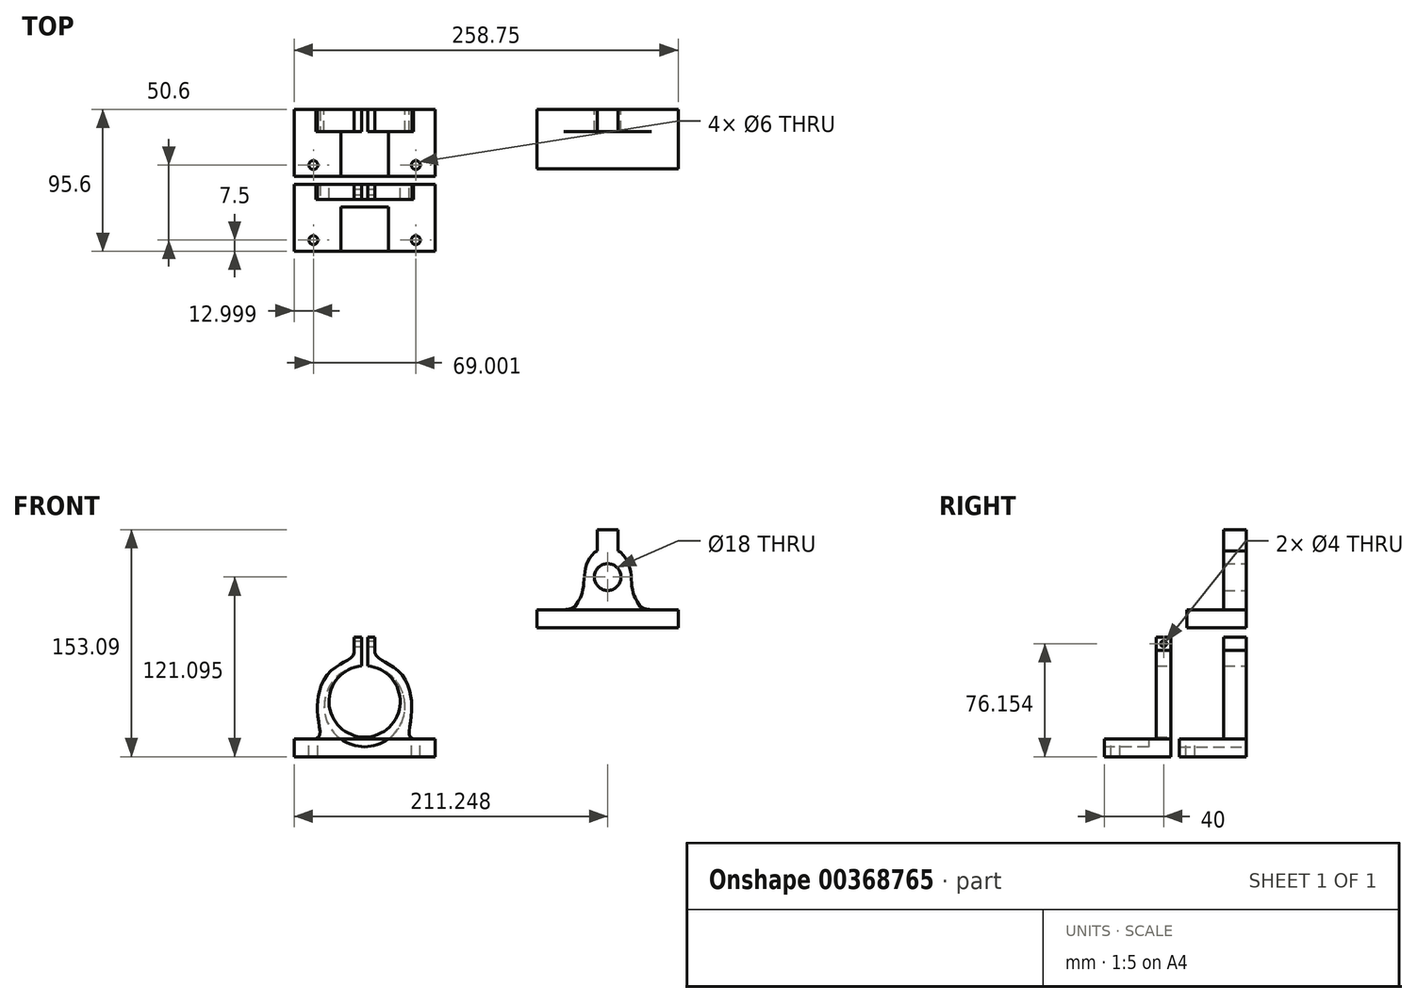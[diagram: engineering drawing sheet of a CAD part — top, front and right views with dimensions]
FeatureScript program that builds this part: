
annotation { "Feature Type Name" : "Feature", "Feature Type Description" : "" }
export const myFeature = defineFeature(function(context is Context, id is Id, definition is map)
    precondition{}
    {
        {
            var Q0;
            Q0=qCreatedBy(makeId("Front.planeOp"),FACE);
            var sketch = newSketch(context, id + "F0", { "sketchPlane" : qUnion([Q0])});
            skLineSegment(sketch, "E0", {"start": v(-93.8, 148.82) * mm, "end": v(-100.8, 148.82) * mm});
            skLineSegment(sketch, "E1", {"start": v(-100.8, 148.82) * mm, "end": v(-100.8, 134.43) * mm});
            skFitSpline(sketch, "E2", {"points": [v(-100.8, 134.43) * mm, v(-106.63, 128.23) * mm, v(-109.38, 119.14) * mm, v(-110.23, 109.7) * mm, v(-112.07, 103.39) * mm, v(-113.8, 99.96) * mm, v(-117.07, 96.12) * mm, v(-123.3, 94.82) * mm], "startDerivative": vector(-41.03, -17.29) * mm, "endDerivative": vector(-26.14, 0) * mm});
            skLineSegment(sketch, "E3", {"start": v(-123.3, 94.82) * mm, "end": v(-141.3, 94.82) * mm});
            skLineSegment(sketch, "E4", {"start": v(-141.3, 94.82) * mm, "end": v(-141.3, 82.82) * mm});
            skLineSegment(sketch, "E5", {"start": v(-141.3, 82.82) * mm, "end": v(-93.8, 82.82) * mm});
            skLineSegment(sketch, "E6", {"start": v(-93.8, 82.82) * mm, "end": v(-93.8, 107.82) * mm});
            skArc(sketch, "E7", {"start": v(-93.8, 125.82) * mm, "mid": v(-102.8, 116.82) * mm, "end": v(-93.8, 107.82) * mm});
            skLineSegment(sketch, "E8", {"start": v(-93.8, 125.82) * mm, "end": v(-93.8, 148.82) * mm});
            skPoint(sketch, "E9", {"position": v(-128.3, 94.82) * mm});
            skLineSegment(sketch, "E10.MirrorCS", {"start": v(-93.8, 148.82) * mm, "end": v(-86.8, 148.82) * mm});
            skLineSegment(sketch, "E11.MirrorCS", {"start": v(-46.3, 82.82) * mm, "end": v(-93.8, 82.82) * mm});
            skLineSegment(sketch, "E12.MirrorCS", {"start": v(-46.3, 94.82) * mm, "end": v(-46.3, 82.82) * mm});
            skLineSegment(sketch, "E13.MirrorCS", {"start": v(-64.3, 94.82) * mm, "end": v(-46.3, 94.82) * mm});
            skFitSpline(sketch, "E14.MirrorCS", {"points": [v(-86.8, 134.43) * mm, v(-80.95, 128.23) * mm, v(-78.2, 119.14) * mm, v(-77.35, 109.7) * mm, v(-75.52, 103.39) * mm, v(-73.79, 99.96) * mm, v(-70.5, 96.12) * mm, v(-64.3, 94.82) * mm], "startDerivative": vector(41.03, -17.29) * mm, "endDerivative": vector(26.14, 0) * mm});
            skLineSegment(sketch, "E15.MirrorCS", {"start": v(-86.8, 148.82) * mm, "end": v(-86.8, 134.43) * mm});
            skArc(sketch, "E16.MirrorCS", {"start": v(-93.8, 125.82) * mm, "mid": v(-84.8, 116.82) * mm, "end": v(-93.8, 107.82) * mm});
            skPoint(sketch, "E17.MirrorP", {"position": v(-59.3, 94.82) * mm});
            skCircle(sketch, "E18", {"center": v(-257.54, 29.73) * mm, "radius": 27.25 * mm});
            skFitSpline(sketch, "E19", {"points": [v(-290.46, 7.73) * mm, v(-287.85, 9.94) * mm, v(-287.98, 16.09) * mm, v(-289.33, 27.52) * mm, v(-288.47, 37.36) * mm, v(-283.92, 49.4) * mm, v(-274.33, 57.89) * mm, v(-268.3, 61.2) * mm, v(-264.74, 65.02) * mm, v(-264.54, 67.48) * mm], "startDerivative": vector(50.74, 19) * mm, "endDerivative": vector(1.63, 36.85) * mm});
            skLineSegment(sketch, "E20", {"start": v(-264.54, 67.48) * mm, "end": v(-264.54, 76.3) * mm});
            skLineSegment(sketch, "E21", {"start": v(-264.54, 76.3) * mm, "end": v(-259.54, 76.3) * mm});
            skLineSegment(sketch, "E22", {"start": v(-259.54, 76.3) * mm, "end": v(-259.54, 56.9) * mm});
            skLineSegment(sketch, "E23", {"start": v(-290.46, 7.73) * mm, "end": v(-305.04, 7.73) * mm});
            skLineSegment(sketch, "E24", {"start": v(-305.04, 7.73) * mm, "end": v(-305.04, -4.27) * mm});
            skLineSegment(sketch, "E25", {"start": v(-305.04, -4.27) * mm, "end": v(-257.6, -4.27) * mm});
            skLineSegment(sketch, "E26", {"start": v(-257.6, -4.27) * mm, "end": v(-257.6, 2.48) * mm});
            skLineSegment(sketch, "E27.MirrorCS", {"start": v(-250.54, 67.48) * mm, "end": v(-250.54, 76.3) * mm});
            skLineSegment(sketch, "E28.MirrorCS", {"start": v(-250.54, 76.3) * mm, "end": v(-255.54, 76.3) * mm});
            skLineSegment(sketch, "E29.MirrorCS", {"start": v(-255.54, 76.3) * mm, "end": v(-255.54, 56.9) * mm});
            skLineSegment(sketch, "E30.MirrorCS", {"start": v(-210.04, -4.27) * mm, "end": v(-257.48, -4.27) * mm});
            skLineSegment(sketch, "E31.MirrorCS", {"start": v(-210.04, 7.73) * mm, "end": v(-210.04, -4.27) * mm});
            skFitSpline(sketch, "E32.MirrorCS", {"points": [v(-224.63, 7.73) * mm, v(-227.23, 9.94) * mm, v(-227.1, 16.09) * mm, v(-225.75, 27.52) * mm, v(-226.61, 37.36) * mm, v(-231.16, 49.4) * mm, v(-240.75, 57.89) * mm, v(-246.78, 61.2) * mm, v(-250.34, 65.02) * mm, v(-250.54, 67.48) * mm], "startDerivative": vector(-50.74, 19) * mm, "endDerivative": vector(-1.63, 36.85) * mm});
            skLineSegment(sketch, "E33.MirrorCS", {"start": v(-224.63, 7.73) * mm, "end": v(-210.04, 7.73) * mm});
            skLineSegment(sketch, "E34", {"start": v(-305.04, -4.27) * mm, "end": v(-210.04, -4.27) * mm});
            skSolve(sketch);
        }
        {
            var Q0;
            Q0=makeQuery(id+"F0.imprint","IMPRINT",FACE,{"disambiguationData":[TD([[makeQuery(id+"F0.imprint","IMPRINT",EDGE,{"derivedFrom":sQuery(id+"F0.wireOp",EDGE,"E6")}),-1.0]])]});
            var Q1;
            Q1=makeQuery(id+"F0.imprint","IMPRINT",FACE,{"disambiguationData":[TD([[makeQuery(id+"F0.imprint","IMPRINT",EDGE,{"derivedFrom":sQuery(id+"F0.wireOp",EDGE,"E0")}),1.0]])]});
            var Q2;
            Q2=makeQuery(id+"F0.imprint","IMPRINT",FACE,{"disambiguationData":[TD([[makeQuery(id+"F0.imprint","IMPRINT",EDGE,{"derivedFrom":sQuery(id+"F0.wireOp",EDGE,"E19")}),-1.0]])]});
            var Q3;
            {var subQ1=sQuery(id+"F0.wireOp",EDGE,"E26");Q3=makeQuery(id+"F0.imprint","IMPRINT",FACE,{"disambiguationData":[TD([[makeQuery(id+"F0.imprint","IMPRINT",EDGE,{"derivedFrom":subQ1}),-1.0]])]});}
            extrude(context, id + "F1", {"entities" : qUnion([Q0, Q1, Q2, Q3]), "depth" : 15 * mm, "offsetDistance" : 25 * mm});
        }
        {
            var Q0;
            Q0=makeQuery(id+"F1.opExtrude","CAP_FACE",FACE,{"disambiguationData":[OSD([sQuery(id+"F0.wireOp",EDGE,"E0"),sQuery(id+"F0.wireOp",EDGE,"E1"),sQuery(id+"F0.wireOp",EDGE,"E2"),sQuery(id+"F0.wireOp",EDGE,"E3"),sQuery(id+"F0.wireOp",EDGE,"E4"),sQuery(id+"F0.wireOp",EDGE,"E5"),sQuery(id+"F0.wireOp",EDGE,"E7"),sQuery(id+"F0.wireOp",EDGE,"E10.MirrorCS"),sQuery(id+"F0.wireOp",EDGE,"E11.MirrorCS"),sQuery(id+"F0.wireOp",EDGE,"E12.MirrorCS"),sQuery(id+"F0.wireOp",EDGE,"E13.MirrorCS"),sQuery(id+"F0.wireOp",EDGE,"E14.MirrorCS"),sQuery(id+"F0.wireOp",EDGE,"E15.MirrorCS"),sQuery(id+"F0.wireOp",EDGE,"E16.MirrorCS")])],"isStart":false});
            var sketch = newSketch(context, id + "F2", { "sketchPlane" : qUnion([Q0])});
            skLineSegment(sketch, "E35.bottom", {"start": v(-141.3, 82.82) * mm, "end": v(-46.3, 82.82) * mm});
            skLineSegment(sketch, "E35.top", {"start": v(-141.3, 94.82) * mm, "end": v(-46.3, 94.82) * mm});
            skLineSegment(sketch, "E35.left", {"start": v(-141.3, 82.82) * mm, "end": v(-141.3, 94.82) * mm});
            skLineSegment(sketch, "E35.right", {"start": v(-46.3, 82.82) * mm, "end": v(-46.3, 94.82) * mm});
            skSolve(sketch);
        }
        {
            var Q0;
            Q0 = qSketchRegion(id + "F2", true);
            extrude(context, id + "F3", {"entities" : qUnion([Q0]), "operationType" : NewBodyOperationType.ADD, "depth" : 25 * mm, "offsetDistance" : 25 * mm});
        }
        {
            var Q0;
            Q0=makeQuery(id+"F1.opExtrude","CAP_FACE",FACE,{"disambiguationData":[OSD([sQuery(id+"F0.wireOp",EDGE,"E19"),sQuery(id+"F0.wireOp",EDGE,"E20"),sQuery(id+"F0.wireOp",EDGE,"E21"),sQuery(id+"F0.wireOp",EDGE,"E22"),sQuery(id+"F0.wireOp",EDGE,"E23"),sQuery(id+"F0.wireOp",EDGE,"E24"),sQuery(id+"F0.wireOp",EDGE,"E29.MirrorCS"),sQuery(id+"F0.wireOp",EDGE,"E27.MirrorCS"),sQuery(id+"F0.wireOp",EDGE,"E28.MirrorCS"),sQuery(id+"F0.wireOp",EDGE,"E31.MirrorCS"),sQuery(id+"F0.wireOp",EDGE,"E32.MirrorCS"),sQuery(id+"F0.wireOp",EDGE,"E18"),sQuery(id+"F0.wireOp",EDGE,"E33.MirrorCS"),sQuery(id+"F0.wireOp",EDGE,"E34")])],"isStart":false});
            var sketch = newSketch(context, id + "F4", { "sketchPlane" : qUnion([Q0])});
            skLineSegment(sketch, "E36.bottom", {"start": v(-305.04, -4.27) * mm, "end": v(-210.04, -4.27) * mm});
            skLineSegment(sketch, "E36.top", {"start": v(-305.04, 7.73) * mm, "end": v(-210.04, 7.73) * mm});
            skLineSegment(sketch, "E36.left", {"start": v(-305.04, -4.27) * mm, "end": v(-305.04, 7.73) * mm});
            skLineSegment(sketch, "E36.right", {"start": v(-210.04, -4.27) * mm, "end": v(-210.04, 7.73) * mm});
            skSolve(sketch);
        }
        {
            var Q0;
            Q0=makeQuery(id+"F4.imprint","IMPRINT",FACE,{"disambiguationData":[TD([[makeQuery(id+"F4.imprint","IMPRINT",EDGE,{"derivedFrom":sQuery(id+"F4.wireOp",EDGE,"E36.bottom")}),1.0]])]});
            extrude(context, id + "F5", {"entities" : qUnion([Q0]), "operationType" : NewBodyOperationType.ADD, "depth" : 30 * mm, "offsetDistance" : 25 * mm});
        }
        {
            var Q0;
            {var subQ0=sQuery(id+"F4.wireOp",EDGE,"E36.top");Q0=makeQuery(id+"F5.boolean.opBoolean","MERGE",FACE,{"derivedFrom":[makeQuery(id+"F1.opExtrude","SWEPT_FACE",FACE,{"disambiguationData":[OSD([sQuery(id+"F0.wireOp",EDGE,"E23")])]}),makeQuery(id+"F5.opExtrude","SWEPT_FACE",FACE,{"disambiguationData":[OSD([subQ0]),TDD([makeQuery(id+"F4.imprint","IMPRINT",EDGE,{"disambiguationData":[TD([[makeQuery(id+"F4.imprint","INTERSECT",VERTEX,{"disambiguationData":[OD(0.0)],"derivedFrom":[makeQuery(id+"F1.opExtrude","CAP_EDGE",EDGE,{"disambiguationData":[OSD([sQuery(id+"F0.wireOp",EDGE,"E18")])],"isStart":false}),subQ0]}),1.0]])],"derivedFrom":subQ0}),makeQuery(id+"F4.imprint","IMPRINT",EDGE,{"disambiguationData":[TD([[makeQuery(id+"F4.imprint","INTERSECT",VERTEX,{"derivedFrom":[subQ0,sQuery(id+"F4.wireOp",EDGE,"E36.left")]}),1.0]])],"derivedFrom":subQ0})])]})]});}
            var sketch = newSketch(context, id + "F6", { "sketchPlane" : qUnion([Q0])});
            skCircle(sketch, "E37", {"center": v(-292.04, -37.5) * mm, "radius": 3 * mm});
            skCircle(sketch, "E38", {"center": v(-223.04, -37.5) * mm, "radius": 3 * mm});
            skLineSegment(sketch, "E39.bottom", {"start": v(-305.04, -45) * mm, "end": v(-210.04, -45) * mm});
            skLineSegment(sketch, "E39.top", {"start": v(-305.04, -30) * mm, "end": v(-210.04, -30) * mm});
            skLineSegment(sketch, "E39.left", {"start": v(-305.04, -45) * mm, "end": v(-305.04, -30) * mm});
            skLineSegment(sketch, "E39.right", {"start": v(-210.04, -45) * mm, "end": v(-210.04, -30) * mm});
            skPoint(sketch, "E40", {"position": v(-305.04, -37.5) * mm});
            skSolve(sketch);
        }
        {
            var Q0;
            Q0=makeQuery(id+"F6.imprint","IMPRINT",FACE,{"disambiguationData":[TD([[makeQuery(id+"F6.imprint","IMPRINT",EDGE,{"derivedFrom":sQuery(id+"F6.wireOp",EDGE,"E37")}),1.0]])]});
            var Q1;
            Q1=makeQuery(id+"F6.imprint","IMPRINT",FACE,{"disambiguationData":[TD([[makeQuery(id+"F6.imprint","IMPRINT",EDGE,{"derivedFrom":sQuery(id+"F6.wireOp",EDGE,"E38")}),1.0]])]});
            extrude(context, id + "F7", {"entities" : qUnion([Q0, Q1]), "operationType" : NewBodyOperationType.REMOVE, "oppositeDirection" : true, "depth" : 25 * mm, "offsetDistance" : 25 * mm});
        }
        {
            var Q0;
            Q0=qCreatedBy(makeId("Front.planeOp"),FACE);
            cPlane(context, id + "F8", {"entities" : qUnion([Q0]), "cplaneType" : CPlaneType.OFFSET, "offset" : 50.6 * mm, "width" : 150 * mm, "height" : 150 * mm});
        }
        {
            var Q0;
            Q0=qCreatedBy(id+"F8.planeOp",FACE);
            var sketch = newSketch(context, id + "F9", { "sketchPlane" : qUnion([Q0])});
            skFitSpline(sketch, "E41", {"points": [v(-290.46, 7.73) * mm, v(-287.85, 9.94) * mm, v(-287.98, 16.09) * mm, v(-289.33, 27.52) * mm, v(-288.47, 37.36) * mm, v(-283.92, 49.4) * mm, v(-274.33, 57.89) * mm, v(-268.3, 61.2) * mm, v(-264.74, 65.02) * mm, v(-264.54, 67.48) * mm], "startDerivative": vector(50.74, 19) * mm, "endDerivative": vector(1.63, 36.85) * mm});
            skLineSegment(sketch, "E42", {"start": v(-264.54, 67.48) * mm, "end": v(-264.54, 76.3) * mm});
            skLineSegment(sketch, "E43", {"start": v(-264.54, 76.3) * mm, "end": v(-259.54, 76.3) * mm});
            skLineSegment(sketch, "E44", {"start": v(-259.54, 76.3) * mm, "end": v(-259.54, 56.9) * mm});
            skLineSegment(sketch, "E45", {"start": v(-290.46, 7.73) * mm, "end": v(-305.04, 7.73) * mm});
            skLineSegment(sketch, "E46", {"start": v(-305.04, 7.73) * mm, "end": v(-305.04, -4.27) * mm});
            skLineSegment(sketch, "E47", {"start": v(-305.04, -4.27) * mm, "end": v(-257.6, -4.27) * mm});
            skLineSegment(sketch, "E48.MirrorCS", {"start": v(-250.54, 67.48) * mm, "end": v(-250.54, 76.3) * mm});
            skLineSegment(sketch, "E49.MirrorCS", {"start": v(-250.54, 76.3) * mm, "end": v(-255.54, 76.3) * mm});
            skLineSegment(sketch, "E50.MirrorCS", {"start": v(-255.54, 76.3) * mm, "end": v(-255.54, 56.9) * mm});
            skLineSegment(sketch, "E51.MirrorCS", {"start": v(-210.04, -4.27) * mm, "end": v(-257.54, -4.27) * mm});
            skLineSegment(sketch, "E52.MirrorCS", {"start": v(-210.04, 7.73) * mm, "end": v(-210.04, -4.27) * mm});
            skFitSpline(sketch, "E53.MirrorCS", {"points": [v(-224.62, 7.73) * mm, v(-227.23, 9.94) * mm, v(-227.1, 16.09) * mm, v(-225.75, 27.52) * mm, v(-226.61, 37.36) * mm, v(-231.16, 49.4) * mm, v(-240.75, 57.89) * mm, v(-246.78, 61.2) * mm, v(-250.34, 65.02) * mm, v(-250.54, 67.48) * mm], "startDerivative": vector(-50.74, 19) * mm, "endDerivative": vector(-1.63, 36.85) * mm});
            skLineSegment(sketch, "E54.MirrorCS", {"start": v(-224.62, 7.73) * mm, "end": v(-210.04, 7.73) * mm});
            skLineSegment(sketch, "E55", {"start": v(-305.04, -4.27) * mm, "end": v(-210.04, -4.27) * mm});
            skArc(sketch, "E56", {"start": v(-259.54, 56.9) * mm, "mid": v(-257.54, 8.99) * mm, "end": v(-255.54, 56.9) * mm});
            skPoint(sketch, "E57.center.orphan", {"position": v(-257.54, 29.74) * mm});
            skLineSegment(sketch, "E58", {"start": v(-290.46, 7.73) * mm, "end": v(-224.62, 7.73) * mm});
            skSolve(sketch);
        }
        {
            var Q0;
            Q0=makeQuery(id+"F9.imprint","IMPRINT",FACE,{"disambiguationData":[TD([[makeQuery(id+"F9.imprint","IMPRINT",EDGE,{"derivedFrom":sQuery(id+"F9.wireOp",EDGE,"E41")}),-1.0]])]});
            extrude(context, id + "F10", {"entities" : qUnion([Q0]), "depth" : 10 * mm, "offsetDistance" : 25 * mm});
        }
        {
            var Q0;
            Q0=makeQuery(id+"F9.imprint","IMPRINT",FACE,{"disambiguationData":[TD([[makeQuery(id+"F9.imprint","IMPRINT",EDGE,{"derivedFrom":sQuery(id+"F9.wireOp",EDGE,"E45")}),1.0]])]});
            extrude(context, id + "F11", {"entities" : qUnion([Q0]), "operationType" : NewBodyOperationType.ADD, "depth" : 45 * mm, "offsetDistance" : 25 * mm});
        }
        {
            var Q0;
            Q0=makeQuery(id+"F11.opExtrude","SWEPT_FACE",FACE,{"disambiguationData":[OSD([sQuery(id+"F9.wireOp",EDGE,"E45"),sQuery(id+"F9.wireOp",EDGE,"E54.MirrorCS"),sQuery(id+"F9.wireOp",EDGE,"E58")])]});
            var sketch = newSketch(context, id + "F12", { "sketchPlane" : qUnion([Q0])});
            skCircle(sketch, "E59", {"center": v(-292.04, -88.1) * mm, "radius": 3 * mm});
            skCircle(sketch, "E60", {"center": v(-223.04, -88.1) * mm, "radius": 3 * mm});
            skLineSegment(sketch, "E61.bottom", {"start": v(-305.04, -95.6) * mm, "end": v(-210.04, -95.6) * mm});
            skLineSegment(sketch, "E61.top", {"start": v(-305.04, -80.6) * mm, "end": v(-210.04, -80.6) * mm});
            skLineSegment(sketch, "E61.left", {"start": v(-305.04, -95.6) * mm, "end": v(-305.04, -80.6) * mm});
            skLineSegment(sketch, "E61.right", {"start": v(-210.04, -95.6) * mm, "end": v(-210.04, -80.6) * mm});
            skPoint(sketch, "E62", {"position": v(-305.04, -88.1) * mm});
            skSolve(sketch);
        }
        {
            var Q0;
            Q0=makeQuery(id+"F12.imprint","IMPRINT",FACE,{"disambiguationData":[TD([[makeQuery(id+"F12.imprint","IMPRINT",EDGE,{"derivedFrom":sQuery(id+"F12.wireOp",EDGE,"E59")}),1.0]])]});
            var Q1;
            Q1=makeQuery(id+"F12.imprint","IMPRINT",FACE,{"disambiguationData":[TD([[makeQuery(id+"F12.imprint","IMPRINT",EDGE,{"derivedFrom":sQuery(id+"F12.wireOp",EDGE,"E60")}),1.0]])]});
            extrude(context, id + "F13", {"entities" : qUnion([Q0, Q1]), "operationType" : NewBodyOperationType.REMOVE, "oppositeDirection" : true, "depth" : 25 * mm, "offsetDistance" : 25 * mm});
        }
        {
            var Q0;
            Q0=makeQuery(id+"F10.opExtrude","SWEPT_FACE",FACE,{"disambiguationData":[OSD([sQuery(id+"F9.wireOp",EDGE,"E48.MirrorCS")])]});
            var sketch = newSketch(context, id + "F14", { "sketchPlane" : qUnion([Q0])});
            skCircle(sketch, "E63", {"center": v(-55.6, 71.88) * mm, "radius": 2 * mm});
            skPoint(sketch, "E63.centerSnap0", {"position": v(-55.6, 67.48) * mm});
            skPoint(sketch, "E63.centerSnap1", {"position": v(-60.6, 71.88) * mm});
            skSolve(sketch);
        }
        {
            var Q0;
            Q0 = qSketchRegion(id + "F14", true);
            extrude(context, id + "F15", {"entities" : qUnion([Q0]), "operationType" : NewBodyOperationType.REMOVE, "oppositeDirection" : true, "depth" : 25 * mm, "offsetDistance" : 25 * mm});
        }
        {
            var Q0;
            Q0=makeQuery(id+"F11.opExtrude","CAP_FACE",FACE,{"disambiguationData":[OSD([sQuery(id+"F9.wireOp",EDGE,"E45"),sQuery(id+"F9.wireOp",EDGE,"E46"),sQuery(id+"F9.wireOp",EDGE,"E47"),sQuery(id+"F9.wireOp",EDGE,"E51.MirrorCS"),sQuery(id+"F9.wireOp",EDGE,"E52.MirrorCS"),sQuery(id+"F9.wireOp",EDGE,"E54.MirrorCS"),sQuery(id+"F9.wireOp",EDGE,"E55"),sQuery(id+"F9.wireOp",EDGE,"E58")])],"isStart":false});
            var sketch = newSketch(context, id + "F16", { "sketchPlane" : qUnion([Q0])});
            skCircle(sketch, "E64", {"center": v(-257.54, 29.74) * mm, "radius": 27.25 * mm});
            skSolve(sketch);
        }
        {
            var Q0;
            Q0 = qSketchRegion(id + "F16", true);
            extrude(context, id + "F17", {"entities" : qUnion([Q0]), "operationType" : NewBodyOperationType.REMOVE, "oppositeDirection" : true, "depth" : 30 * mm, "offsetDistance" : 25 * mm});
        }
    });
